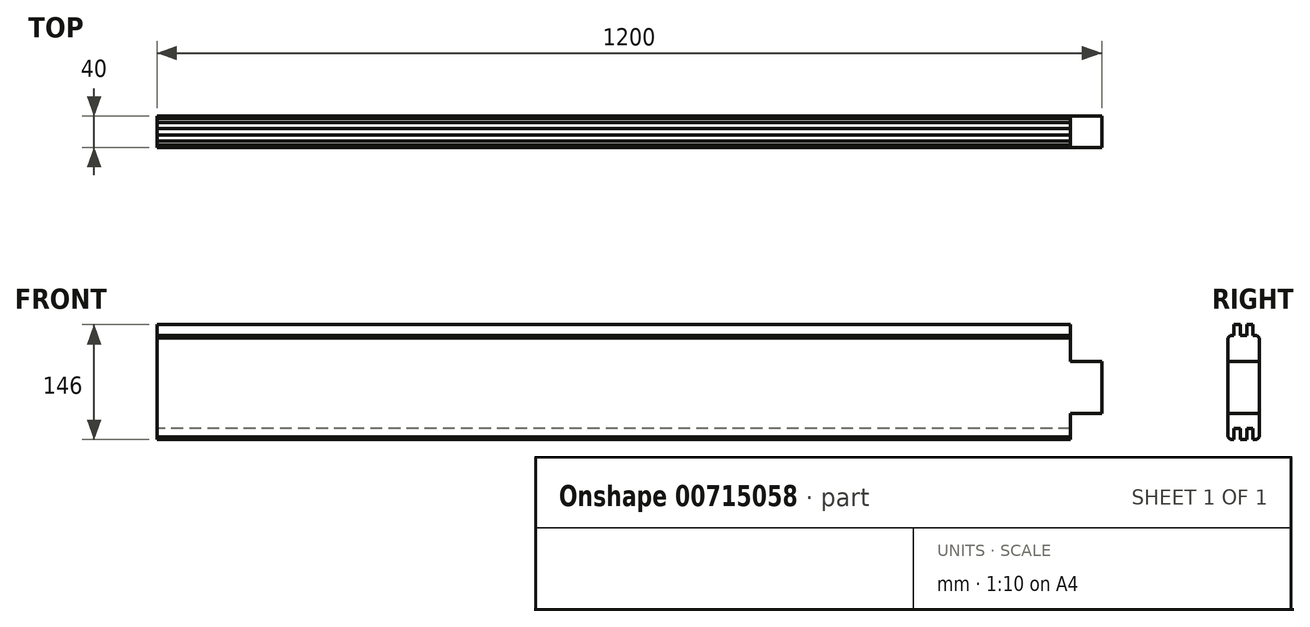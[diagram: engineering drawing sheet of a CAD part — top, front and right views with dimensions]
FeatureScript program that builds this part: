
annotation { "Feature Type Name" : "Feature", "Feature Type Description" : "" }
export const myFeature = defineFeature(function(context is Context, id is Id, definition is map)
    precondition{}
    {
        {
            assignVariable(context, id + "F0", {"name" : "Laenge", "anyValue" : 1200});
        }
        {
            var Q0;
            Q0=qCreatedBy(makeId("Right.planeOp"),FACE);
            var sketch = newSketch(context, id + "F1", { "sketchPlane" : qUnion([Q0])});
            skLineSegment(sketch, "E0", {"start": v(20, 63) * mm, "end": v(20, -63) * mm});
            skLineSegment(sketch, "E1", {"start": v(20, -63) * mm, "end": v(17, -66) * mm});
            skLineSegment(sketch, "E2", {"start": v(17, -66) * mm, "end": v(12, -66) * mm});
            skLineSegment(sketch, "E3", {"start": v(12, -52) * mm, "end": v(12, -66) * mm});
            skLineSegment(sketch, "E4", {"start": v(12, -52) * mm, "end": v(4, -52) * mm});
            skLineSegment(sketch, "E5", {"start": v(4, -66) * mm, "end": v(4, -52) * mm});
            skLineSegment(sketch, "E6", {"start": v(4, -66) * mm, "end": v(-4, -66) * mm});
            skLineSegment(sketch, "E7", {"start": v(-4, -52) * mm, "end": v(-4, -66) * mm});
            skLineSegment(sketch, "E8", {"start": v(-4, -52) * mm, "end": v(-12, -52) * mm});
            skLineSegment(sketch, "E9", {"start": v(-12, -66) * mm, "end": v(-12, -52) * mm});
            skLineSegment(sketch, "E10", {"start": v(-12, -66) * mm, "end": v(-17, -66) * mm});
            skLineSegment(sketch, "E11", {"start": v(-17, -66) * mm, "end": v(-20, -63) * mm});
            skLineSegment(sketch, "E12", {"start": v(-20, -63) * mm, "end": v(-20, 63) * mm});
            skLineSegment(sketch, "E13", {"start": v(-20, 63) * mm, "end": v(-17, 66) * mm});
            skLineSegment(sketch, "E14", {"start": v(-17, 66) * mm, "end": v(-12, 66) * mm});
            skLineSegment(sketch, "E15", {"start": v(-4, 66) * mm, "end": v(4, 66) * mm});
            skLineSegment(sketch, "E16", {"start": v(12, 66) * mm, "end": v(17, 66) * mm});
            skLineSegment(sketch, "E17", {"start": v(17, 66) * mm, "end": v(20, 63) * mm});
            skPoint(sketch, "E18.end.orphan", {"position": v(12, 57.8) * mm});
            skPoint(sketch, "E19.end.orphan", {"position": v(4, 66.3) * mm});
            skPoint(sketch, "E20.end.orphan", {"position": v(-4, 66.3) * mm});
            skLineSegment(sketch, "E21", {"start": v(-12, 66) * mm, "end": v(-12, 80) * mm});
            skLineSegment(sketch, "E22", {"start": v(-12, 80) * mm, "end": v(-4, 80) * mm});
            skLineSegment(sketch, "E23", {"start": v(-4, 80) * mm, "end": v(-4, 66) * mm});
            skLineSegment(sketch, "E24", {"start": v(4, 66) * mm, "end": v(4, 80) * mm});
            skLineSegment(sketch, "E25", {"start": v(4, 80) * mm, "end": v(12, 80) * mm});
            skLineSegment(sketch, "E26", {"start": v(12, 80) * mm, "end": v(12, 66) * mm});
            skLineSegment(sketch, "E27", {"start": v(20, -33) * mm, "end": v(-20, -33) * mm});
            skLineSegment(sketch, "E28", {"start": v(20, 33) * mm, "end": v(-20, 33) * mm});
            skPoint(sketch, "E29.end.orphan", {"position": v(-141.42, 0) * mm});
            skLineSegment(sketch, "E30", {"start": v(20, 0) * mm, "end": v(-20, 0) * mm});
            skLineSegment(sketch, "E31", {"start": v(20, 0) * mm, "end": v(-20, 0) * mm, "construction": true});
            skLineSegment(sketch, "E32", {"start": v(0, 33) * mm, "end": v(0, -33) * mm, "construction": true});
            skSolve(sketch);
        }
        {
            var Q0;
            Q0=qCreatedBy(makeId("Front.planeOp"),FACE);
            var sketch = newSketch(context, id + "F2", { "sketchPlane" : qUnion([Q0])});
            skLineSegment(sketch, "E33", {"start": v(600, 0) * mm, "end": v(-600, 0) * mm, "construction": true});
            skPoint(sketch, "E34.right.start.orphan", {"position": v(-259.12, 108.1) * mm});
            skPoint(sketch, "E35.left.start.orphan", {"position": v(237.35, 108.1) * mm});
            skPoint(sketch, "E36.left.end.orphan", {"position": v(237.35, -84.05) * mm});
            skPoint(sketch, "E36.bottom.start.orphan", {"position": v(237.35, -117.05) * mm});
            skPoint(sketch, "E37.right.start.orphan", {"position": v(-259.12, -117.05) * mm});
            skPoint(sketch, "E37.top.end.orphan", {"position": v(-259.12, -84.05) * mm});
            skLineSegment(sketch, "E38.bottom", {"start": v(-640, 33) * mm, "end": v(-560, 33) * mm});
            skLineSegment(sketch, "E38.top", {"start": v(-640, 133) * mm, "end": v(-560, 133) * mm});
            skLineSegment(sketch, "E38.left", {"start": v(-640, 33) * mm, "end": v(-640, 133) * mm});
            skLineSegment(sketch, "E38.right", {"start": v(-560, 33) * mm, "end": v(-560, 133) * mm});
            skPoint(sketch, "E38.middle", {"position": v(-600, 83) * mm});
            skLineSegment(sketch, "E39.bottom", {"start": v(-640, -133) * mm, "end": v(-560, -133) * mm});
            skLineSegment(sketch, "E39.top", {"start": v(-640, -33) * mm, "end": v(-560, -33) * mm});
            skLineSegment(sketch, "E39.left", {"start": v(-640, -133) * mm, "end": v(-640, -33) * mm});
            skLineSegment(sketch, "E39.right", {"start": v(-560, -133) * mm, "end": v(-560, -33) * mm});
            skPoint(sketch, "E39.middle", {"position": v(-600, -83) * mm});
            skLineSegment(sketch, "E40.bottom", {"start": v(640, 33) * mm, "end": v(560, 33) * mm});
            skLineSegment(sketch, "E40.top", {"start": v(640, 133) * mm, "end": v(560, 133) * mm});
            skLineSegment(sketch, "E40.left", {"start": v(640, 33) * mm, "end": v(640, 133) * mm});
            skLineSegment(sketch, "E40.right", {"start": v(560, 33) * mm, "end": v(560, 133) * mm});
            skPoint(sketch, "E40.middle", {"position": v(600, 83) * mm});
            skLineSegment(sketch, "E41.bottom", {"start": v(640, -33) * mm, "end": v(560, -33) * mm});
            skLineSegment(sketch, "E41.top", {"start": v(640, -133) * mm, "end": v(560, -133) * mm});
            skLineSegment(sketch, "E41.left", {"start": v(640, -33) * mm, "end": v(640, -133) * mm});
            skLineSegment(sketch, "E41.right", {"start": v(560, -33) * mm, "end": v(560, -133) * mm});
            skPoint(sketch, "E41.middle", {"position": v(600, -83) * mm});
            skSolve(sketch);
        }
        {
            var Q0;
            {var subQ3=sQuery(id+"F1.wireOp",EDGE,"E13");Q0=makeQuery(id+"F1.imprint","IMPRINT",FACE,{"disambiguationData":[TD([[makeQuery(id+"F1.imprint","IMPRINT",EDGE,{"derivedFrom":subQ3}),-1.0]])]});}
            var Q1;
            {var subQ0=sQuery(id+"F1.wireOp",EDGE,"E28");Q1=makeQuery(id+"F1.imprint","IMPRINT",FACE,{"disambiguationData":[TD([[makeQuery(id+"F1.imprint","IMPRINT",EDGE,{"derivedFrom":subQ0}),1.0]])]});}
            var Q2;
            {var subQ0=sQuery(id+"F1.wireOp",EDGE,"E27");Q2=makeQuery(id+"F1.imprint","IMPRINT",FACE,{"disambiguationData":[TD([[makeQuery(id+"F1.imprint","IMPRINT",EDGE,{"derivedFrom":subQ0}),-1.0]])]});}
            var Q3;
            {var subQ1=sQuery(id+"F1.wireOp",EDGE,"E1");Q3=makeQuery(id+"F1.imprint","IMPRINT",FACE,{"disambiguationData":[TD([[makeQuery(id+"F1.imprint","IMPRINT",EDGE,{"derivedFrom":subQ1}),-1.0]])]});}
            extrude(context, id + "F3", {"entities" : qUnion([Q0, Q1, Q2, Q3]), "endBound" : BoundingType.SYMMETRIC, "depth" : getVariable(context, 'Laenge') * mm, "offsetDistance" : 25 * mm});
        }
        {
            var Q0;
            Q0=makeQuery(id+"F2.imprint","IMPRINT",FACE,{"disambiguationData":[TD([[makeQuery(id+"F2.imprint","IMPRINT",EDGE,{"derivedFrom":sQuery(id+"F2.wireOp",EDGE,"E40.bottom")}),-1.0]])]});
            var Q1;
            Q1=makeQuery(id+"F2.imprint","IMPRINT",FACE,{"disambiguationData":[TD([[makeQuery(id+"F2.imprint","IMPRINT",EDGE,{"derivedFrom":sQuery(id+"F2.wireOp",EDGE,"E41.bottom")}),1.0]])]});
            extrude(context, id + "F4", {"entities" : qUnion([Q0, Q1]), "operationType" : NewBodyOperationType.REMOVE, "endBound" : BoundingType.SYMMETRIC, "oppositeDirection" : true, "depth" : 50 * mm, "offsetDistance" : 25 * mm});
        }
    });
